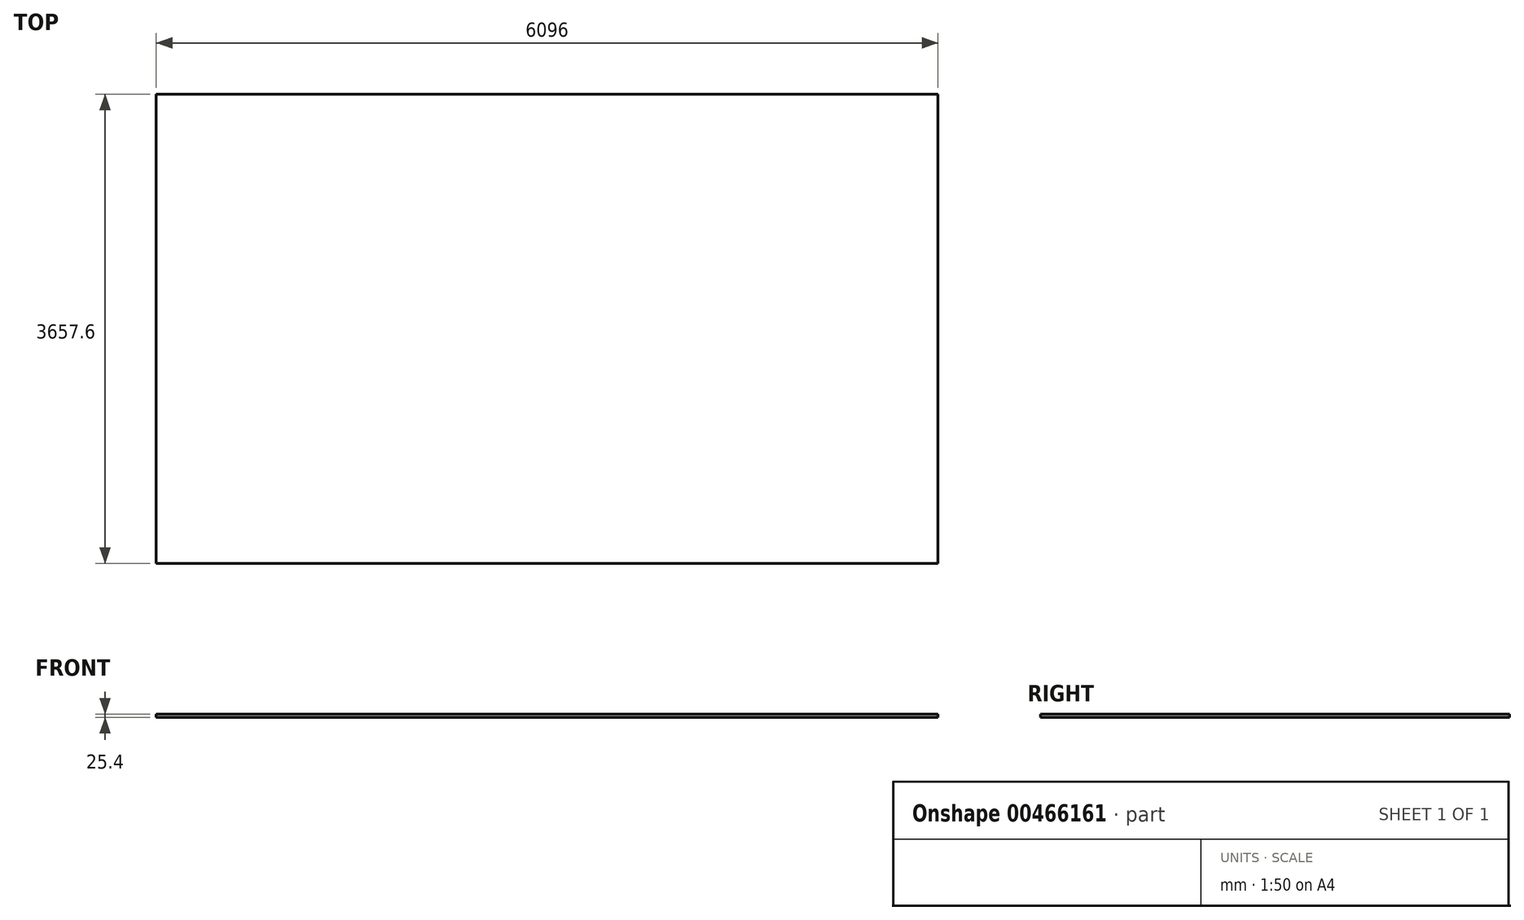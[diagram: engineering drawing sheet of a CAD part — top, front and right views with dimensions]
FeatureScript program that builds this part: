
annotation { "Feature Type Name" : "Feature", "Feature Type Description" : "" }
export const myFeature = defineFeature(function(context is Context, id is Id, definition is map)
    precondition{}
    {
        {
            var Q0;
            Q0=qCreatedBy(makeId("Top.planeOp"),FACE);
            var sketch = newSketch(context, id + "F0", { "sketchPlane" : qUnion([Q0])});
            skLineSegment(sketch, "E0.bottom", {"start": v(-1370.27, 0) * mm, "end": v(4725.73, 0) * mm});
            skLineSegment(sketch, "E0.top", {"start": v(-1370.27, -3657.6) * mm, "end": v(4725.73, -3657.6) * mm});
            skLineSegment(sketch, "E0.left", {"start": v(-1370.27, 0) * mm, "end": v(-1370.27, -3657.6) * mm});
            skLineSegment(sketch, "E0.right", {"start": v(4725.73, 0) * mm, "end": v(4725.73, -3657.6) * mm});
            skSolve(sketch);
        }
        {
            var Q0;
            Q0=makeQuery(id+"F0.imprint","IMPRINT",FACE,{"disambiguationData":[TD([[makeQuery(id+"F0.imprint","IMPRINT",EDGE,{"derivedFrom":sQuery(id+"F0.wireOp",EDGE,"E0.bottom")}),-1.0]])]});
            extrude(context, id + "F1", {"entities" : qUnion([Q0]), "depth" : 25.4 * mm});
        }
    });
